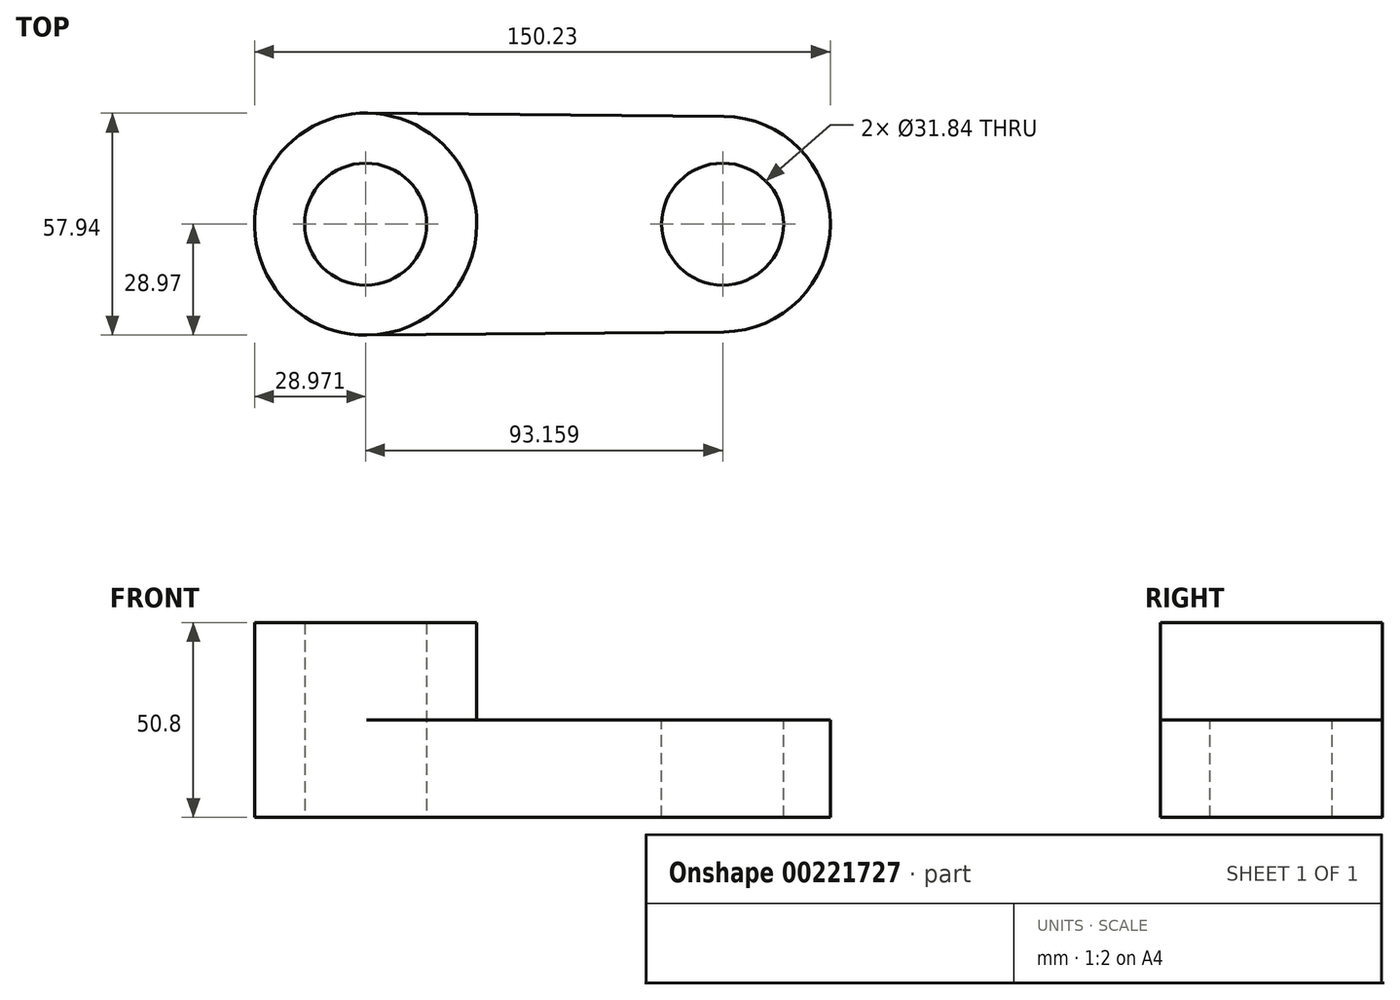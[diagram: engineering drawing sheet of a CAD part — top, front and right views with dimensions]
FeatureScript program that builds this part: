
annotation { "Feature Type Name" : "Feature", "Feature Type Description" : "" }
export const myFeature = defineFeature(function(context is Context, id is Id, definition is map)
    precondition{}
    {
        {
            var Q0;
            Q0=qCreatedBy(makeId("Top.planeOp"),FACE);
            var sketch = newSketch(context, id + "F0", { "sketchPlane" : qUnion([Q0])});
            skCircle(sketch, "E0", {"center": v(-46.58, 0) * mm, "radius": 15.92 * mm});
            skCircle(sketch, "E1", {"center": v(46.58, 0) * mm, "radius": 15.92 * mm});
            skArc(sketch, "E2", {"start": v(-46.3, 28.97) * mm, "mid": v(-75.55, 0) * mm, "end": v(-46.3, -28.97) * mm});
            skArc(sketch, "E3", {"start": v(46.84, -28.1) * mm, "mid": v(74.68, 0) * mm, "end": v(46.84, 28.1) * mm});
            skLineSegment(sketch, "E4", {"start": v(-46.3, 28.97) * mm, "end": v(46.84, 28.1) * mm});
            skLineSegment(sketch, "E5", {"start": v(46.84, -28.1) * mm, "end": v(-46.3, -28.97) * mm});
            skArc(sketch, "E6", {"start": v(-46.3, -28.97) * mm, "mid": v(-17.6, 0) * mm, "end": v(-46.3, 28.97) * mm});
            skSolve(sketch);
        }
        {
            var Q0;
            Q0=makeQuery(id+"F0.imprint","IMPRINT",FACE,{"disambiguationData":[TD([[makeQuery(id+"F0.imprint","IMPRINT",EDGE,{"derivedFrom":sQuery(id+"F0.wireOp",EDGE,"E0")}),-1.0]])]});
            extrude(context, id + "F1", {"entities" : qUnion([Q0]), "depth" : 25.4 * mm});
        }
        {
            var Q0;
            Q0=makeQuery(id+"F0.imprint","IMPRINT",FACE,{"disambiguationData":[TD([[makeQuery(id+"F0.imprint","IMPRINT",EDGE,{"derivedFrom":sQuery(id+"F0.wireOp",EDGE,"E1")}),-1.0]])]});
            var Q1;
            Q1=makeQuery(id+"F0.imprint","IMPRINT",FACE,{"disambiguationData":[TD([[makeQuery(id+"F0.imprint","IMPRINT",EDGE,{"derivedFrom":sQuery(id+"F0.wireOp",EDGE,"E0")}),-1.0]])]});
            extrude(context, id + "F2", {"entities" : qUnion([Q0, Q1]), "operationType" : NewBodyOperationType.ADD, "oppositeDirection" : true, "depth" : 25.4 * mm});
        }
    });
